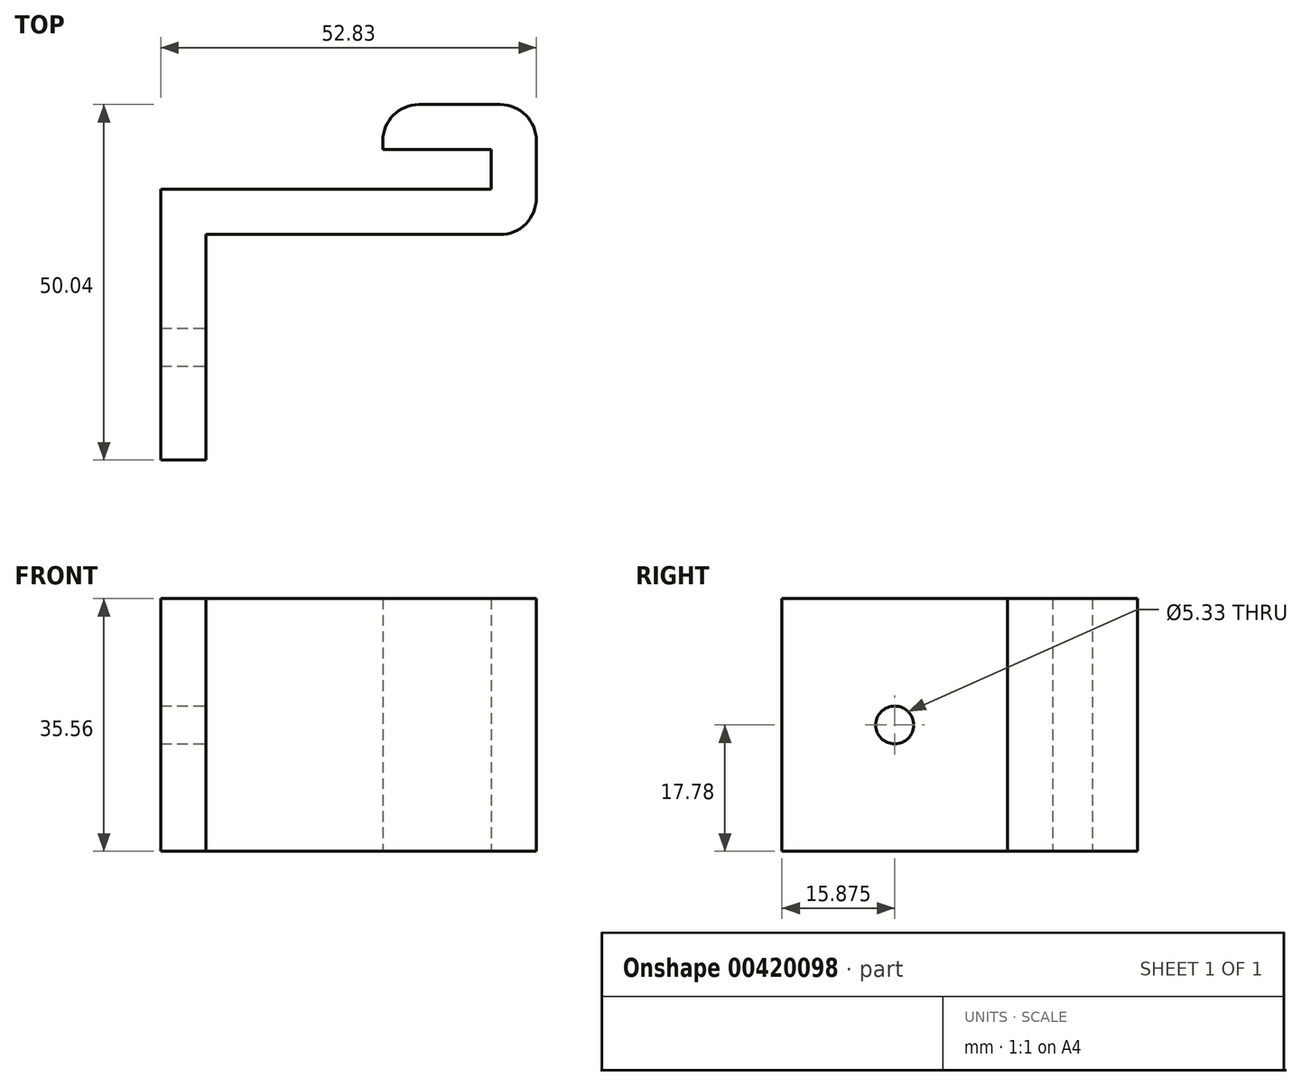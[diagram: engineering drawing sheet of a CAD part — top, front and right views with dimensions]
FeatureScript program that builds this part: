
annotation { "Feature Type Name" : "Feature", "Feature Type Description" : "" }
export const myFeature = defineFeature(function(context is Context, id is Id, definition is map)
    precondition{}
    {
        {
            var Q0;
            Q0=qCreatedBy(makeId("Top.planeOp"),FACE);
            var sketch = newSketch(context, id + "F0", { "sketchPlane" : qUnion([Q0])});
            skLineSegment(sketch, "E0", {"start": v(0, 0) * mm, "end": v(-46.48, 0) * mm});
            skLineSegment(sketch, "E1", {"start": v(0, 0) * mm, "end": v(0, 18.29) * mm});
            skLineSegment(sketch, "E2", {"start": v(0, 18.29) * mm, "end": v(-21.59, 18.29) * mm});
            skLineSegment(sketch, "E3", {"start": v(-21.6, 18.29) * mm, "end": v(-21.6, 11.94) * mm});
            skLineSegment(sketch, "E4", {"start": v(-21.59, 11.94) * mm, "end": v(-6.35, 11.94) * mm});
            skLineSegment(sketch, "E5", {"start": v(-6.35, 11.94) * mm, "end": v(-6.35, 6.35) * mm});
            skLineSegment(sketch, "E6", {"start": v(-6.35, 6.35) * mm, "end": v(-52.83, 6.35) * mm});
            skLineSegment(sketch, "E7", {"start": v(-52.83, 6.35) * mm, "end": v(-52.83, -31.75) * mm});
            skLineSegment(sketch, "E8", {"start": v(-52.83, -31.75) * mm, "end": v(-46.48, -31.75) * mm});
            skLineSegment(sketch, "E9", {"start": v(-46.48, -31.75) * mm, "end": v(-46.48, 0) * mm});
            skSolve(sketch);
        }
        {
            var Q0;
            Q0=makeQuery(id+"F0.imprint","IMPRINT",FACE,{"disambiguationData":[TD([[makeQuery(id+"F0.imprint","IMPRINT",EDGE,{"derivedFrom":sQuery(id+"F0.wireOp",EDGE,"E0")}),-1.0]])]});
            extrude(context, id + "F1", {"entities" : qUnion([Q0]), "depth" : 35.56 * mm});
        }
        {
            var Q0;
            Q0=makeQuery(id+"F1.opExtrude","SWEPT_FACE",FACE,{"disambiguationData":[OSD([sQuery(id+"F0.wireOp",EDGE,"E9")])]});
            var sketch = newSketch(context, id + "F2", { "sketchPlane" : qUnion([Q0])});
            skLineSegment(sketch, "E10", {"start": v(-15.87, 35.56) * mm, "end": v(-15.87, 0) * mm, "construction": true});
            skLineSegment(sketch, "E11", {"start": v(0, 17.78) * mm, "end": v(-31.75, 17.78) * mm, "construction": true});
            skCircle(sketch, "E12", {"center": v(-15.87, 17.78) * mm, "radius": 2.67 * mm});
            skSolve(sketch);
        }
        {
            var Q0;
            Q0=makeQuery(id+"F2.imprint","IMPRINT",FACE,{"disambiguationData":[TD([[makeQuery(id+"F2.imprint","IMPRINT",EDGE,{"derivedFrom":sQuery(id+"F2.wireOp",EDGE,"E12")}),1.0]])]});
            extrude(context, id + "F3", {"entities" : qUnion([Q0]), "operationType" : NewBodyOperationType.REMOVE, "oppositeDirection" : true, "depth" : 25.4 * mm});
        }
        {
            var Q0;
            Q0=makeQuery(id+"F1.opExtrude","SWEPT_EDGE",EDGE,{"disambiguationData":[OSD([sQuery(id+"F0.wireOp",EDGE,"E0"),sQuery(id+"F0.wireOp",EDGE,"E1")])]});
            var Q1;
            Q1=makeQuery(id+"F1.opExtrude","SWEPT_EDGE",EDGE,{"disambiguationData":[OSD([sQuery(id+"F0.wireOp",EDGE,"E1"),sQuery(id+"F0.wireOp",EDGE,"E2")])]});
            var Q2;
            Q2=makeQuery(id+"F1.opExtrude","SWEPT_EDGE",EDGE,{"disambiguationData":[OSD([sQuery(id+"F0.wireOp",EDGE,"E2"),sQuery(id+"F0.wireOp",EDGE,"E3")])]});
            fillet(context, id + "F4", {"entities" : qUnion([Q0, Q1, Q2]), "radius" : 5.08 * mm, "tangentPropagation" : true, "allowEdgeOverflow" : false});
        }
    });
